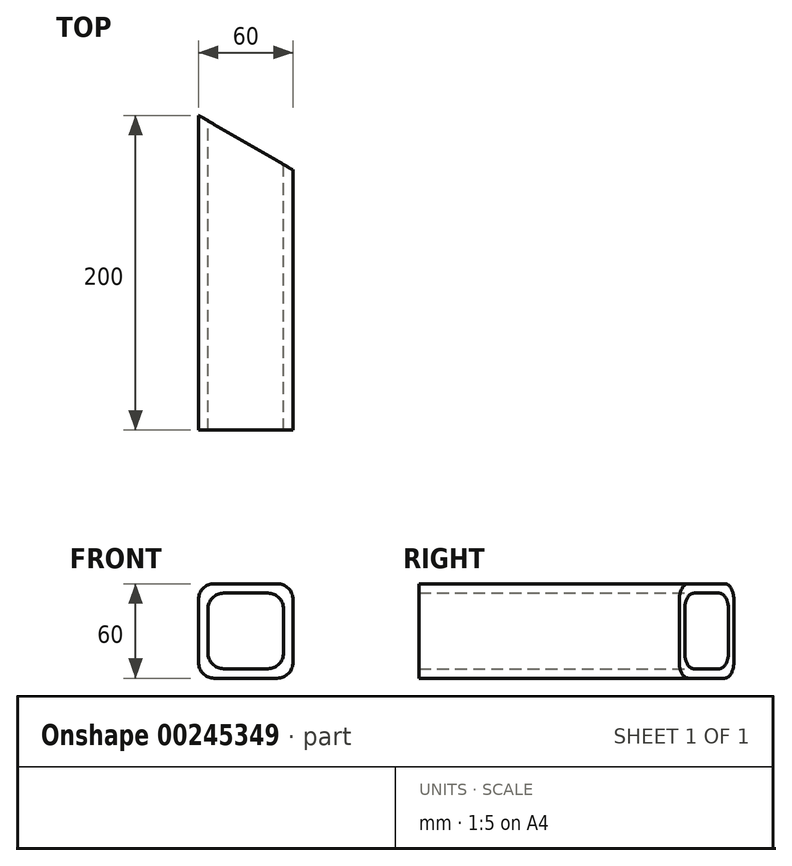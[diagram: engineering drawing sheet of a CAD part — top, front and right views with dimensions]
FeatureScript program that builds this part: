
annotation { "Feature Type Name" : "Feature", "Feature Type Description" : "" }
export const myFeature = defineFeature(function(context is Context, id is Id, definition is map)
    precondition{}
    {
        {
            var Q0;
            Q0=qCreatedBy(makeId("Front.planeOp"),FACE);
            var sketch = newSketch(context, id + "F0", { "sketchPlane" : qUnion([Q0])});
            skLineSegment(sketch, "E0.bottom", {"start": v(0, 0) * mm, "end": v(60, 0) * mm});
            skLineSegment(sketch, "E0.top", {"start": v(0, 60) * mm, "end": v(60, 60) * mm});
            skLineSegment(sketch, "E0.left", {"start": v(0, 0) * mm, "end": v(0, 60) * mm});
            skLineSegment(sketch, "E0.right", {"start": v(60, 0) * mm, "end": v(60, 60) * mm});
            skSolve(sketch);
        }
        {
            var Q0;
            Q0 = qSketchRegion(id + "F0", true);
            extrude(context, id + "F1", {"entities" : qUnion([Q0]), "depth" : 200 * mm});
        }
        {
            var Q0;
            Q0=makeQuery(id+"F1.opExtrude","CAP_FACE",FACE,{"disambiguationData":[OSD([sQuery(id+"F0.wireOp",EDGE,"E0.bottom"),sQuery(id+"F0.wireOp",EDGE,"E0.top"),sQuery(id+"F0.wireOp",EDGE,"E0.left"),sQuery(id+"F0.wireOp",EDGE,"E0.right")])],"isStart":false});
            var Q1;
            Q1=makeQuery(id+"F1.opExtrude","CAP_FACE",FACE,{"disambiguationData":[OSD([sQuery(id+"F0.wireOp",EDGE,"E0.bottom"),sQuery(id+"F0.wireOp",EDGE,"E0.top"),sQuery(id+"F0.wireOp",EDGE,"E0.left"),sQuery(id+"F0.wireOp",EDGE,"E0.right")])],"isStart":true});
            shell(context, id + "F2", {"entities" : qUnion([Q0, Q1]), "thickness" : 6 * mm});
        }
        {
            var Q0;
            Q0=makeQuery(id+"F1.opExtrude","SWEPT_EDGE",EDGE,{"disambiguationData":[OSD([sQuery(id+"F0.wireOp",EDGE,"E0.top"),sQuery(id+"F0.wireOp",EDGE,"E0.right")])]});
            var Q1;
            Q1=makeQuery(id+"F1.opExtrude","SWEPT_EDGE",EDGE,{"disambiguationData":[OSD([sQuery(id+"F0.wireOp",EDGE,"E0.top"),sQuery(id+"F0.wireOp",EDGE,"E0.left")])]});
            var Q2;
            Q2=makeQuery(id+"F1.opExtrude","SWEPT_EDGE",EDGE,{"disambiguationData":[OSD([sQuery(id+"F0.wireOp",EDGE,"E0.bottom"),sQuery(id+"F0.wireOp",EDGE,"E0.right")])]});
            var Q3;
            Q3=makeQuery(id+"F2.opShell","OFFSET_EDGE",EDGE,{"disambiguationData":[OSD([sQuery(id+"F0.wireOp",EDGE,"E0.bottom"),sQuery(id+"F0.wireOp",EDGE,"E0.left")])]});
            var Q4;
            Q4=makeQuery(id+"F1.opExtrude","SWEPT_EDGE",EDGE,{"disambiguationData":[OSD([sQuery(id+"F0.wireOp",EDGE,"E0.bottom"),sQuery(id+"F0.wireOp",EDGE,"E0.left")])]});
            var Q5;
            Q5=makeQuery(id+"F2.opShell","OFFSET_EDGE",EDGE,{"disambiguationData":[OSD([sQuery(id+"F0.wireOp",EDGE,"E0.bottom"),sQuery(id+"F0.wireOp",EDGE,"E0.right")])]});
            var Q6;
            Q6=makeQuery(id+"F2.opShell","OFFSET_EDGE",EDGE,{"disambiguationData":[OSD([sQuery(id+"F0.wireOp",EDGE,"E0.top"),sQuery(id+"F0.wireOp",EDGE,"E0.right")])]});
            var Q7;
            Q7=makeQuery(id+"F2.opShell","OFFSET_EDGE",EDGE,{"disambiguationData":[OSD([sQuery(id+"F0.wireOp",EDGE,"E0.top"),sQuery(id+"F0.wireOp",EDGE,"E0.left")])]});
            fillet(context, id + "F3", {"entities" : qUnion([Q0, Q1, Q2, Q3, Q4, Q5, Q6, Q7]), "radius" : 10 * mm, "tangentPropagation" : true, "allowEdgeOverflow" : false});
        }
        {
            var Q0;
            Q0=makeQuery(id+"F1.opExtrude","SWEPT_FACE",FACE,{"disambiguationData":[OSD([sQuery(id+"F0.wireOp",EDGE,"E0.top")])]});
            var sketch = newSketch(context, id + "F4", { "sketchPlane" : qUnion([Q0])});
            skLineSegment(sketch, "E1", {"start": v(70, -40.41) * mm, "end": v(0, 0) * mm});
            skLineSegment(sketch, "E2", {"start": v(0, 0) * mm, "end": v(70, 0) * mm});
            skLineSegment(sketch, "E3", {"start": v(70, 0) * mm, "end": v(70, -40.41) * mm});
            skSolve(sketch);
        }
        {
            var Q0;
            Q0 = qSketchRegion(id + "F4", true);
            extrude(context, id + "F5", {"entities" : qUnion([Q0]), "operationType" : NewBodyOperationType.REMOVE, "endBound" : BoundingType.THROUGH_ALL, "oppositeDirection" : true, "depth" : 25 * mm});
        }
    });
